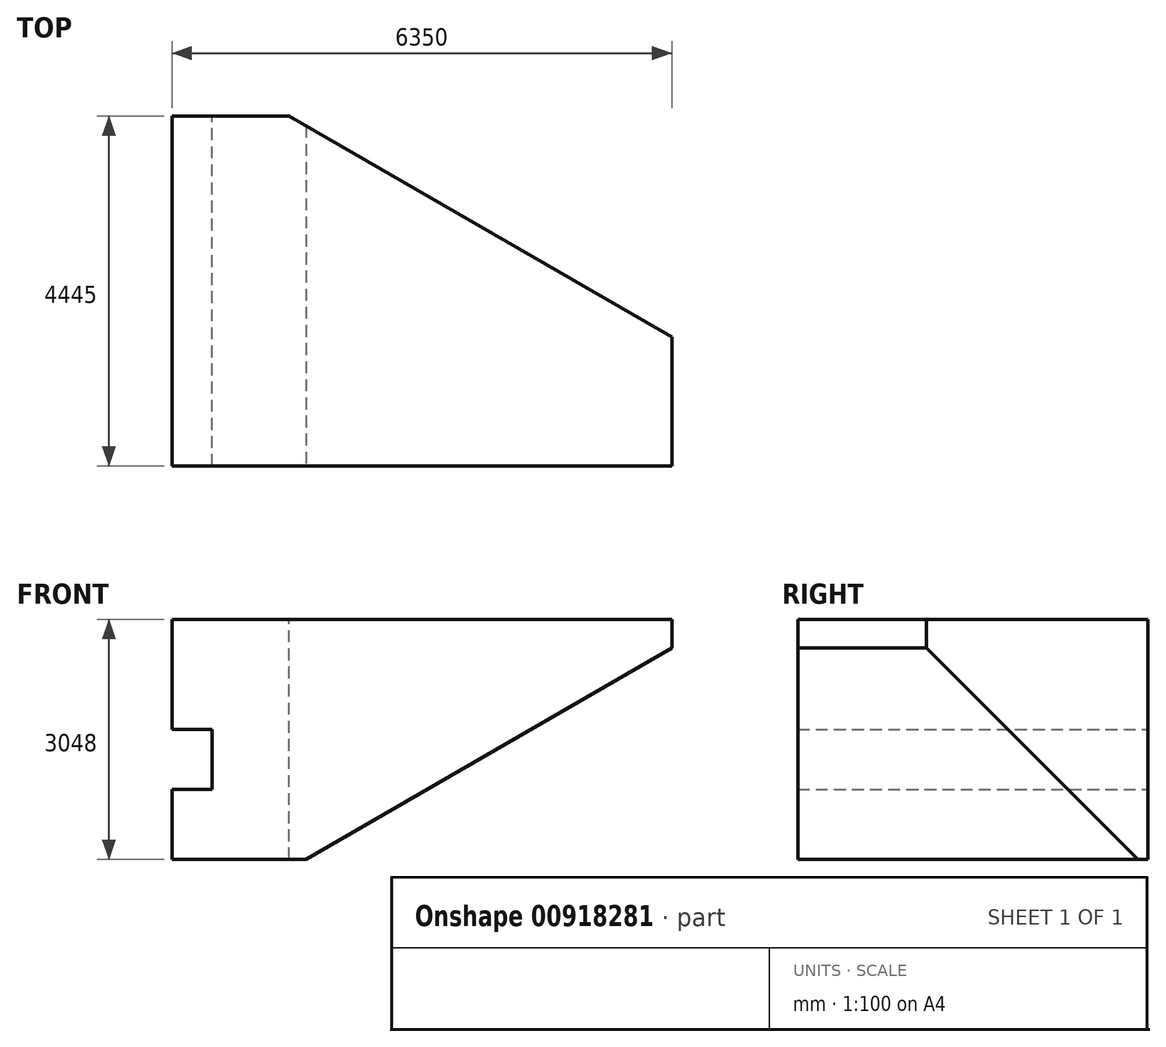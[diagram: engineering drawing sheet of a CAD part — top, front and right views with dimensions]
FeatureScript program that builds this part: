
annotation { "Feature Type Name" : "Feature", "Feature Type Description" : "" }
export const myFeature = defineFeature(function(context is Context, id is Id, definition is map)
    precondition{}
    {
        {
            var Q0;
            Q0=qCreatedBy(makeId("Front.planeOp"),FACE);
            var sketch = newSketch(context, id + "F0", { "sketchPlane" : qUnion([Q0])});
            skLineSegment(sketch, "E0.bottom", {"start": v(-1018.32, 1148.97) * mm, "end": v(886.68, 1148.97) * mm});
            skLineSegment(sketch, "E0.top", {"start": v(-1018.32, -1899.03) * mm, "end": v(886.68, -1899.03) * mm});
            skLineSegment(sketch, "E0.left", {"start": v(-1018.32, 1148.97) * mm, "end": v(-1018.32, -248.03) * mm});
            skLineSegment(sketch, "E0.right", {"start": v(886.68, 1148.97) * mm, "end": v(886.68, -1899.03) * mm});
            skLineSegment(sketch, "E1", {"start": v(-1018.32, -1010.03) * mm, "end": v(-510.32, -1010.03) * mm});
            skLineSegment(sketch, "E2", {"start": v(-1018.32, -248.03) * mm, "end": v(-510.32, -248.03) * mm});
            skLineSegment(sketch, "E3.trimOffspring", {"start": v(-1018.32, -1010.03) * mm, "end": v(-1018.32, -1899.03) * mm});
            skLineSegment(sketch, "E4.trimOffspring", {"start": v(-510.32, -248.03) * mm, "end": v(-510.32, -1010.03) * mm});
            skSolve(sketch);
        }
        {
            var Q0;
            Q0=makeQuery(id+"F0.imprint","IMPRINT",FACE,{"disambiguationData":[TD([[makeQuery(id+"F0.imprint","IMPRINT",EDGE,{"derivedFrom":sQuery(id+"F0.wireOp",EDGE,"E0.bottom")}),-1.0]])]});
            extrude(context, id + "F1", {"entities" : qUnion([Q0]), "depth" : 4445 * mm, "offsetDistance" : 25.4 * mm});
        }
        {
            var Q0;
            Q0=makeQuery(id+"F1.opExtrude","CAP_FACE",FACE,{"disambiguationData":[OSD([sQuery(id+"F0.wireOp",EDGE,"E0.bottom"),sQuery(id+"F0.wireOp",EDGE,"E0.top"),sQuery(id+"F0.wireOp",EDGE,"E0.left"),sQuery(id+"F0.wireOp",EDGE,"E0.right"),sQuery(id+"F0.wireOp",EDGE,"E1"),sQuery(id+"F0.wireOp",EDGE,"E2"),sQuery(id+"F0.wireOp",EDGE,"E3.trimOffspring"),sQuery(id+"F0.wireOp",EDGE,"E4.trimOffspring")])],"isStart":false});
            var sketch = newSketch(context, id + "F2", { "sketchPlane" : qUnion([Q0])});
            skLineSegment(sketch, "E5", {"start": v(886.68, 1148.97) * mm, "end": v(5331.68, 1148.97) * mm});
            skLineSegment(sketch, "E6", {"start": v(886.68, -1899.03) * mm, "end": v(5331.68, -1899.03) * mm});
            skLineSegment(sketch, "E7", {"start": v(5331.68, 1148.97) * mm, "end": v(5331.68, -1899.03) * mm});
            skSolve(sketch);
        }
        {
            var Q0;
            Q0=makeQuery(id+"F2.imprint","IMPRINT",FACE,{"disambiguationData":[TD([[makeQuery(id+"F2.imprint","IMPRINT",EDGE,{"derivedFrom":sQuery(id+"F2.wireOp",EDGE,"E5")}),-1.0]])]});
            extrude(context, id + "F3", {"entities" : qUnion([Q0]), "operationType" : NewBodyOperationType.ADD, "oppositeDirection" : true, "depth" : 4445 * mm, "offsetDistance" : 25.4 * mm});
        }
        {
            var Q0;
            {var subQ0=sQuery(id+"F0.wireOp",EDGE,"E0.right");Q0=makeQuery(id+"F3.boolean.opBoolean","MERGE",FACE,{"derivedFrom":[makeQuery(id+"F1.opExtrude","CAP_FACE",FACE,{"disambiguationData":[OSD([sQuery(id+"F0.wireOp",EDGE,"E0.bottom"),sQuery(id+"F0.wireOp",EDGE,"E0.top"),sQuery(id+"F0.wireOp",EDGE,"E0.left"),subQ0,sQuery(id+"F0.wireOp",EDGE,"E1"),sQuery(id+"F0.wireOp",EDGE,"E2"),sQuery(id+"F0.wireOp",EDGE,"E3.trimOffspring"),sQuery(id+"F0.wireOp",EDGE,"E4.trimOffspring")])],"isStart":false}),makeQuery(id+"F3.opExtrude","CAP_FACE",FACE,{"disambiguationData":[OSD([subQ0,sQuery(id+"F2.wireOp",EDGE,"E5"),sQuery(id+"F2.wireOp",EDGE,"E6"),sQuery(id+"F2.wireOp",EDGE,"E7")])],"isStart":true})]});}
            var sketch = newSketch(context, id + "F4", { "sketchPlane" : qUnion([Q0])});
            skLineSegment(sketch, "E8", {"start": v(683.15, -1899.03) * mm, "end": v(5331.68, 784.8) * mm});
            skSolve(sketch);
        }
        {
            var Q0;
            {var subQ0=sQuery(id+"F4.wireOp",EDGE,"E8");Q0=makeQuery(id+"F4.imprint","IMPRINT",FACE,{"disambiguationData":[TD([[makeQuery(id+"F4.imprint","IMPRINT",EDGE,{"derivedFrom":subQ0}),-1.0]])]});}
            extrude(context, id + "F5", {"entities" : qUnion([Q0]), "operationType" : NewBodyOperationType.REMOVE, "endBound" : BoundingType.THROUGH_ALL, "oppositeDirection" : true, "depth" : 25.4 * mm, "offsetDistance" : 25.4 * mm});
        }
        {
            var Q0;
            Q0=makeQuery(id+"F3.boolean.opBoolean","MERGE",FACE,{"derivedFrom":[makeQuery(id+"F1.opExtrude","SWEPT_FACE",FACE,{"disambiguationData":[OSD([sQuery(id+"F0.wireOp",EDGE,"E0.bottom")])]}),makeQuery(id+"F3.opExtrude","SWEPT_FACE",FACE,{"disambiguationData":[OSD([sQuery(id+"F2.wireOp",EDGE,"E5")])]})]});
            var sketch = newSketch(context, id + "F6", { "sketchPlane" : qUnion([Q0])});
            skLineSegment(sketch, "E9", {"start": v(466.87, 0) * mm, "end": v(5331.68, -2808.7) * mm});
            skSolve(sketch);
        }
        {
            var Q0;
            {var subQ0=sQuery(id+"F6.wireOp",EDGE,"E9");Q0=makeQuery(id+"F6.imprint","IMPRINT",FACE,{"disambiguationData":[TD([[makeQuery(id+"F6.imprint","IMPRINT",EDGE,{"derivedFrom":subQ0}),1.0]])]});}
            extrude(context, id + "F7", {"entities" : qUnion([Q0]), "operationType" : NewBodyOperationType.REMOVE, "endBound" : BoundingType.THROUGH_ALL, "oppositeDirection" : true, "depth" : 25.4 * mm, "offsetDistance" : 25.4 * mm});
        }
    });
